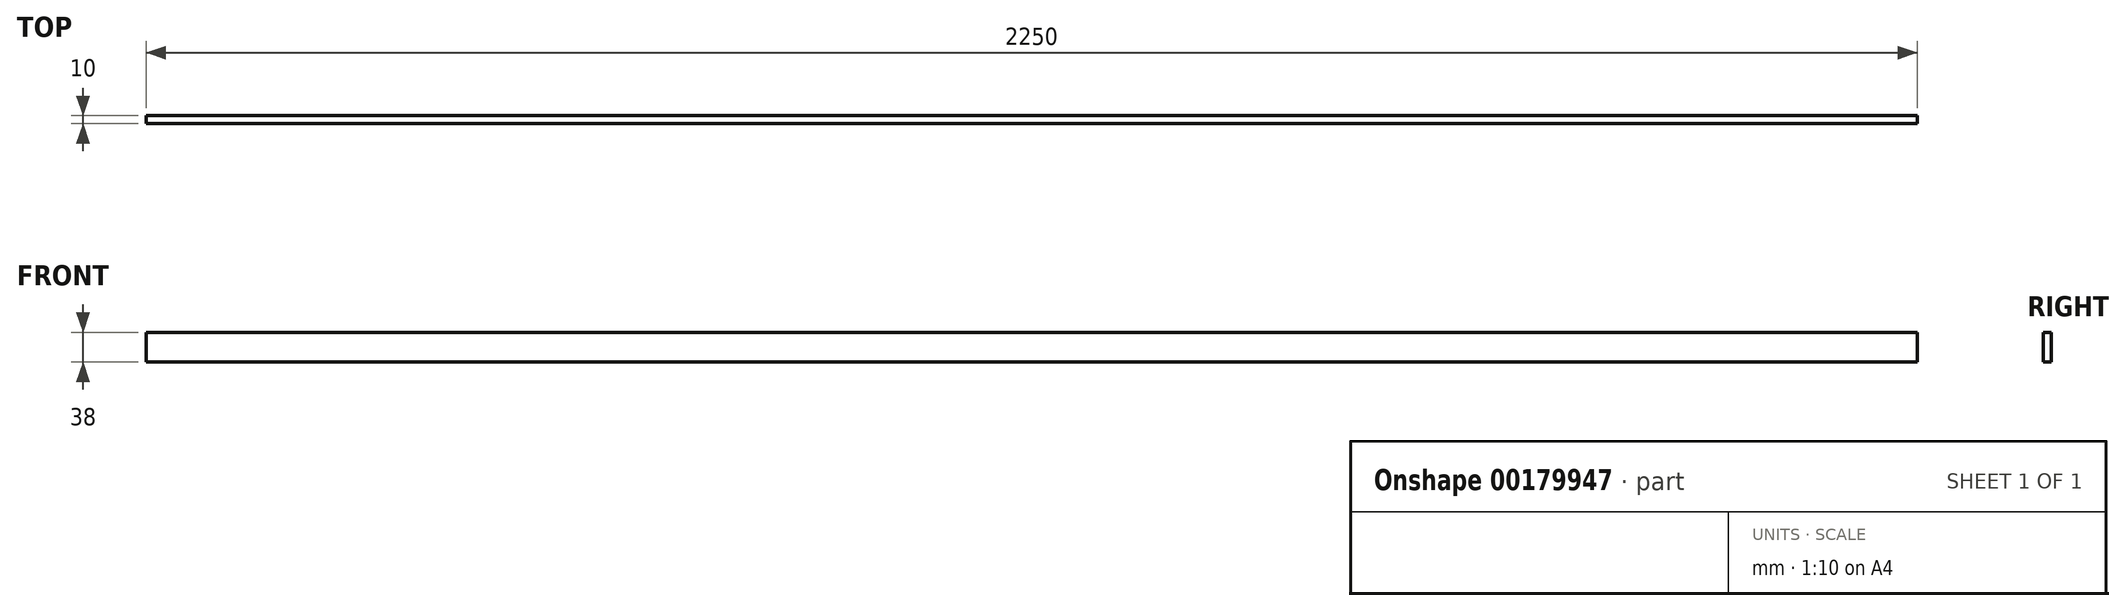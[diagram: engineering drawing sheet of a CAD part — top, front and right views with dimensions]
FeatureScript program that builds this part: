
annotation { "Feature Type Name" : "Feature", "Feature Type Description" : "" }
export const myFeature = defineFeature(function(context is Context, id is Id, definition is map)
    precondition{}
    {
        {
            var Q0;
            Q0=qCreatedBy(makeId("Front.planeOp"),FACE);
            var sketch = newSketch(context, id + "F0", { "sketchPlane" : qUnion([Q0])});
            skLineSegment(sketch, "E0.bottom", {"start": v(0, 0) * mm, "end": v(2250, 0) * mm});
            skLineSegment(sketch, "E0.top", {"start": v(0, 38) * mm, "end": v(2250, 38) * mm});
            skLineSegment(sketch, "E0.left", {"start": v(0, 0) * mm, "end": v(0, 38) * mm});
            skLineSegment(sketch, "E0.right", {"start": v(2250, 0) * mm, "end": v(2250, 38) * mm});
            skSolve(sketch);
        }
        {
            var Q0;
            Q0=qSketchRegion(id+"F0",true);
            extrude(context, id + "F1", {"entities" : qUnion([Q0]), "depth" : 10 * mm});
        }
    });
